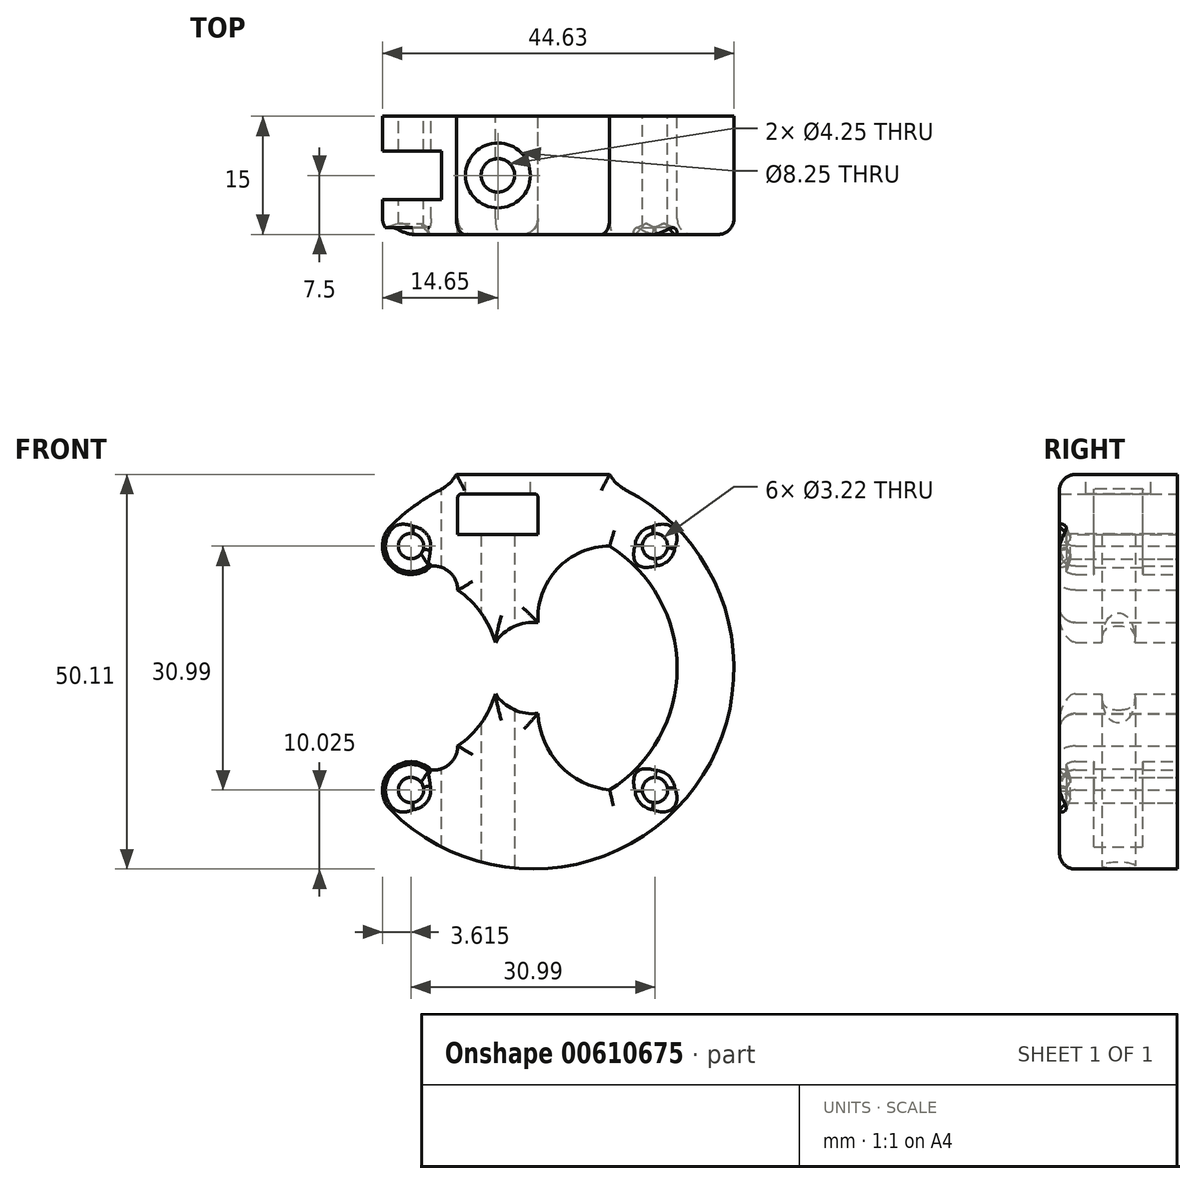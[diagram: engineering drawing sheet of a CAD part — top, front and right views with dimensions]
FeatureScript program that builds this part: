
annotation { "Feature Type Name" : "Feature", "Feature Type Description" : "" }
export const myFeature = defineFeature(function(context is Context, id is Id, definition is map)
    precondition{}
    {
        {
            var Q0;
            Q0=qCreatedBy(makeId("Front.planeOp"),FACE);
            var sketch = newSketch(context, id + "F0", { "sketchPlane" : qUnion([Q0])});
            skLineSegment(sketch, "E0.bottom", {"start": v(15.5, -15.5) * mm, "end": v(-15.5, -15.5) * mm, "construction": true});
            skLineSegment(sketch, "E0.top", {"start": v(15.5, 15.5) * mm, "end": v(-15.5, 15.5) * mm, "construction": true});
            skLineSegment(sketch, "E0.left", {"start": v(15.5, -15.5) * mm, "end": v(15.5, 15.5) * mm, "construction": true});
            skLineSegment(sketch, "E0.right", {"start": v(-15.5, -15.5) * mm, "end": v(-15.5, 15.5) * mm, "construction": true});
            skPoint(sketch, "E0.middle", {"position": v(0, 0) * mm});
            skCircle(sketch, "E1", {"center": v(-15.5, 15.5) * mm, "radius": 1.61 * mm});
            skCircle(sketch, "E2", {"center": v(15.5, 15.5) * mm, "radius": 1.61 * mm});
            skCircle(sketch, "E3", {"center": v(15.5, -15.5) * mm, "radius": 1.61 * mm});
            skCircle(sketch, "E4", {"center": v(-15.5, -15.5) * mm, "radius": 1.61 * mm});
            skArc(sketch, "E5", {"start": v(18.05, 18.05) * mm, "mid": v(14.17, 21.23) * mm, "end": v(9.74, 23.6) * mm});
            skArc(sketch, "E6", {"start": v(12.94, 12.94) * mm, "mid": v(18.05, 12.94) * mm, "end": v(18.05, 18.05) * mm});
            skArc(sketch, "E7", {"start": v(18.05, -18.05) * mm, "mid": v(18.05, -12.94) * mm, "end": v(12.94, -12.94) * mm});
            skArc(sketch, "E8.trimOffspring", {"start": v(-9.74, 15.5) * mm, "mid": v(-18.3, 0) * mm, "end": v(-9.74, -15.5) * mm});
            skLineSegment(sketch, "E9.bottom", {"start": v(-0.64, 22.14) * mm, "end": v(9.56, 22.14) * mm});
            skLineSegment(sketch, "E9.top", {"start": v(-0.64, 16.94) * mm, "end": v(9.56, 16.94) * mm});
            skLineSegment(sketch, "E9.left", {"start": v(-0.64, 22.14) * mm, "end": v(-0.64, 16.94) * mm});
            skLineSegment(sketch, "E9.right", {"start": v(9.56, 22.14) * mm, "end": v(9.56, 16.94) * mm});
            skArc(sketch, "E10.trimOffspring", {"start": v(-9.74, 23.6) * mm, "mid": v(-21.23, -14.17) * mm, "end": v(18.05, -18.05) * mm});
            skLineSegment(sketch, "E11.left", {"start": v(-0.64, 6.98) * mm, "end": v(-0.64, 5.76) * mm});
            skPoint(sketch, "E11.top.end.orphan", {"position": v(9.56, -18.78) * mm});
            skArc(sketch, "E12", {"start": v(-0.64, -5.76) * mm, "mid": v(2.42, -5.27) * mm, "end": v(4.79, -3.27) * mm});
            skArc(sketch, "E13", {"start": v(9.56, 9.9) * mm, "mid": v(6.6, 7) * mm, "end": v(4.79, 3.27) * mm});
            skArc(sketch, "E14.trimOffspring", {"start": v(4.79, -3.27) * mm, "mid": v(6.6, -7) * mm, "end": v(9.56, -9.9) * mm});
            skArc(sketch, "E15.trimOffspring", {"start": v(4.79, 3.27) * mm, "mid": v(2.42, 5.27) * mm, "end": v(-0.64, 5.76) * mm});
            skArc(sketch, "E16", {"start": v(12.94, 12.94) * mm, "mid": v(10.57, 12.18) * mm, "end": v(9.56, 9.9) * mm});
            skArc(sketch, "E17", {"start": v(-0.64, 5.76) * mm, "mid": v(-3.08, 12.6) * mm, "end": v(-9.74, 15.5) * mm});
            skPoint(sketch, "E18.orphan", {"position": v(-0.64, 15.5) * mm});
            skArc(sketch, "E19", {"start": v(9.56, -9.9) * mm, "mid": v(10.57, -12.18) * mm, "end": v(12.94, -12.94) * mm});
            skArc(sketch, "E20", {"start": v(-9.74, -15.5) * mm, "mid": v(-3.4, -12.31) * mm, "end": v(-0.64, -5.76) * mm});
            skLineSegment(sketch, "E21.top", {"start": v(-9.74, 24.6) * mm, "end": v(9.74, 24.6) * mm});
            skLineSegment(sketch, "E21.left", {"start": v(-9.74, 23.6) * mm, "end": v(-9.74, 24.6) * mm});
            skLineSegment(sketch, "E21.right", {"start": v(9.74, 23.6) * mm, "end": v(9.74, 24.6) * mm});
            skSolve(sketch);
        }
        {
            var Q0;
            Q0=makeQuery(id+"F0.imprint","IMPRINT",FACE,{"disambiguationData":[TD([[makeQuery(id+"F0.imprint","IMPRINT",EDGE,{"derivedFrom":sQuery(id+"F0.wireOp",EDGE,"E1")}),-1.0]])]});
            extrude(context, id + "F1", {"entities" : qUnion([Q0]), "depth" : 15 * mm});
        }
        {
            var Q0;
            Q0=makeQuery(id+"F1.opExtrude","SWEPT_EDGE",EDGE,{"disambiguationData":[OSD([sQuery(id+"F0.wireOp",EDGE,"E5"),sQuery(id+"F0.wireOp",EDGE,"E21.right")])]});
            var Q1;
            Q1=makeQuery(id+"F1.opExtrude","SWEPT_EDGE",EDGE,{"disambiguationData":[OSD([sQuery(id+"F0.wireOp",EDGE,"E10.trimOffspring"),sQuery(id+"F0.wireOp",EDGE,"E21.left")])]});
            fillet(context, id + "F2", {"entities" : qUnion([Q0, Q1]), "radius" : 5 * mm, "tangentPropagation" : true, "allowEdgeOverflow" : false});
        }
        {
            var Q0;
            Q0=makeQuery(id+"F1.opExtrude","SWEPT_FACE",FACE,{"disambiguationData":[OSD([sQuery(id+"F0.wireOp",EDGE,"E9.top")])]});
            var sketch = newSketch(context, id + "F3", { "sketchPlane" : qUnion([Q0])});
            skCircle(sketch, "E22", {"center": v(4.46, -7.5) * mm, "radius": 2.12 * mm});
            skPoint(sketch, "E22.centerSnap0", {"position": v(-0.64, -7.5) * mm});
            skPoint(sketch, "E22.centerSnap1", {"position": v(4.46, 0) * mm});
            skSolve(sketch);
        }
        {
            var Q0;
            Q0=makeQuery(id+"F3.imprint","IMPRINT",FACE,{"disambiguationData":[TD([[makeQuery(id+"F3.imprint","IMPRINT",EDGE,{"derivedFrom":sQuery(id+"F3.wireOp",EDGE,"E22")}),1.0]])]});
            extrude(context, id + "F4", {"entities" : qUnion([Q0]), "operationType" : NewBodyOperationType.REMOVE, "endBound" : BoundingType.THROUGH_ALL, "depth" : 60 * mm, "hasSecondDirection" : true, "secondDirectionBound" : SecondDirectionBoundingType.THROUGH_ALL, "secondDirectionOppositeDirection" : true, "secondDirectionDepth" : 25 * mm});
        }
        {
            var Q0;
            Q0=makeQuery(id+"F1.opExtrude","SWEPT_FACE",FACE,{"disambiguationData":[OSD([sQuery(id+"F0.wireOp",EDGE,"E21.top")])]});
            var sketch = newSketch(context, id + "F5", { "sketchPlane" : qUnion([Q0])});
            skCircle(sketch, "E23", {"center": v(4.46, -7.5) * mm, "radius": 4.12 * mm});
            skSolve(sketch);
        }
        {
            var Q0;
            Q0=makeQuery(id+"F5.imprint","IMPRINT",FACE,{"disambiguationData":[TD([[makeQuery(id+"F5.imprint","IMPRINT",EDGE,{"derivedFrom":sQuery(id+"F5.wireOp",EDGE,"E23")}),1.0]])]});
            var Q1;
            Q1=sQuery(id+"F5.wireOp",EDGE,"E23");
            extrude(context, id + "F6", {"entities" : qUnion([Q0]), "operationType" : NewBodyOperationType.REMOVE, "surfaceEntities" : qUnion([Q1]), "endBound" : BoundingType.UP_TO_NEXT, "oppositeDirection" : true, "depth" : 25 * mm});
        }
        {
            var Q0;
            Q0=makeQuery(id+"F1.opExtrude","CAP_EDGE",EDGE,{"disambiguationData":[OSD([sQuery(id+"F0.wireOp",EDGE,"E17")])],"isStart":false});
            var Q1;
            Q1=makeQuery(id+"F1.opExtrude","CAP_EDGE",EDGE,{"disambiguationData":[OSD([sQuery(id+"F0.wireOp",EDGE,"E8.trimOffspring")])],"isStart":false});
            var Q2;
            Q2=makeQuery(id+"F1.opExtrude","CAP_EDGE",EDGE,{"disambiguationData":[OSD([sQuery(id+"F0.wireOp",EDGE,"E15.trimOffspring")])],"isStart":false});
            var Q3;
            Q3=makeQuery(id+"F1.opExtrude","CAP_EDGE",EDGE,{"disambiguationData":[OSD([sQuery(id+"F0.wireOp",EDGE,"E13")])],"isStart":false});
            var Q4;
            Q4=makeQuery(id+"F1.opExtrude","CAP_EDGE",EDGE,{"disambiguationData":[OSD([sQuery(id+"F0.wireOp",EDGE,"E16")])],"isStart":false});
            var Q5;
            Q5=makeQuery(id+"F1.opExtrude","CAP_EDGE",EDGE,{"disambiguationData":[OSD([sQuery(id+"F0.wireOp",EDGE,"E6")])],"isStart":false});
            var Q6;
            Q6=makeQuery(id+"F1.opExtrude","CAP_EDGE",EDGE,{"disambiguationData":[OSD([sQuery(id+"F0.wireOp",EDGE,"E10.trimOffspring")])],"isStart":false});
            var Q7;
            {var subQ0=sQuery(id+"F0.wireOp",EDGE,"E21.left");var subQ1=sQuery(id+"F0.wireOp",EDGE,"E10.trimOffspring");Q7=makeQuery(id+"F2.opFillet","BLEND_EDGE",EDGE,{"blendedFrom":[makeQuery(id+"F1.opExtrude","SWEPT_EDGE",EDGE,{"disambiguationData":[OSD([subQ1,subQ0])]}),makeQuery(id+"F1.opExtrude","CAP_FACE",FACE,{"disambiguationData":[OSD([sQuery(id+"F0.wireOp",EDGE,"E1"),sQuery(id+"F0.wireOp",EDGE,"E2"),sQuery(id+"F0.wireOp",EDGE,"E3"),sQuery(id+"F0.wireOp",EDGE,"E4"),sQuery(id+"F0.wireOp",EDGE,"E5"),sQuery(id+"F0.wireOp",EDGE,"E6"),sQuery(id+"F0.wireOp",EDGE,"E7"),sQuery(id+"F0.wireOp",EDGE,"E8.trimOffspring"),sQuery(id+"F0.wireOp",EDGE,"E9.bottom"),sQuery(id+"F0.wireOp",EDGE,"E9.top"),sQuery(id+"F0.wireOp",EDGE,"E9.left"),sQuery(id+"F0.wireOp",EDGE,"E9.right"),subQ1,sQuery(id+"F0.wireOp",EDGE,"E12"),sQuery(id+"F0.wireOp",EDGE,"E13"),sQuery(id+"F0.wireOp",EDGE,"E14.trimOffspring"),sQuery(id+"F0.wireOp",EDGE,"E15.trimOffspring"),sQuery(id+"F0.wireOp",EDGE,"E16"),sQuery(id+"F0.wireOp",EDGE,"E17"),sQuery(id+"F0.wireOp",EDGE,"E19"),sQuery(id+"F0.wireOp",EDGE,"E20"),sQuery(id+"F0.wireOp",EDGE,"E21.top"),subQ0,sQuery(id+"F0.wireOp",EDGE,"E21.right")])],"isStart":false})],"blendedInto":[makeQuery(id+"F1.opExtrude","CAP_FACE",FACE,{"disambiguationData":[OSD([sQuery(id+"F0.wireOp",EDGE,"E1"),sQuery(id+"F0.wireOp",EDGE,"E2"),sQuery(id+"F0.wireOp",EDGE,"E3"),sQuery(id+"F0.wireOp",EDGE,"E4"),sQuery(id+"F0.wireOp",EDGE,"E5"),sQuery(id+"F0.wireOp",EDGE,"E6"),sQuery(id+"F0.wireOp",EDGE,"E7"),sQuery(id+"F0.wireOp",EDGE,"E8.trimOffspring"),sQuery(id+"F0.wireOp",EDGE,"E9.bottom"),sQuery(id+"F0.wireOp",EDGE,"E9.top"),sQuery(id+"F0.wireOp",EDGE,"E9.left"),sQuery(id+"F0.wireOp",EDGE,"E9.right"),subQ1,sQuery(id+"F0.wireOp",EDGE,"E12"),sQuery(id+"F0.wireOp",EDGE,"E13"),sQuery(id+"F0.wireOp",EDGE,"E14.trimOffspring"),sQuery(id+"F0.wireOp",EDGE,"E15.trimOffspring"),sQuery(id+"F0.wireOp",EDGE,"E16"),sQuery(id+"F0.wireOp",EDGE,"E17"),sQuery(id+"F0.wireOp",EDGE,"E19"),sQuery(id+"F0.wireOp",EDGE,"E20"),sQuery(id+"F0.wireOp",EDGE,"E21.top"),subQ0,sQuery(id+"F0.wireOp",EDGE,"E21.right")])],"isStart":false})]});}
            var Q8;
            Q8=makeQuery(id+"F1.opExtrude","CAP_EDGE",EDGE,{"disambiguationData":[OSD([sQuery(id+"F0.wireOp",EDGE,"E7")])],"isStart":false});
            var Q9;
            Q9=makeQuery(id+"F1.opExtrude","CAP_EDGE",EDGE,{"disambiguationData":[OSD([sQuery(id+"F0.wireOp",EDGE,"E19")])],"isStart":false});
            var Q10;
            Q10=makeQuery(id+"F1.opExtrude","CAP_EDGE",EDGE,{"disambiguationData":[OSD([sQuery(id+"F0.wireOp",EDGE,"E14.trimOffspring")])],"isStart":false});
            var Q11;
            Q11=makeQuery(id+"F1.opExtrude","CAP_EDGE",EDGE,{"disambiguationData":[OSD([sQuery(id+"F0.wireOp",EDGE,"E12")])],"isStart":false});
            var Q12;
            Q12=makeQuery(id+"F1.opExtrude","CAP_EDGE",EDGE,{"disambiguationData":[OSD([sQuery(id+"F0.wireOp",EDGE,"E20")])],"isStart":false});
            var Q13;
            Q13=makeQuery(id+"F1.opExtrude","CAP_EDGE",EDGE,{"disambiguationData":[OSD([sQuery(id+"F0.wireOp",EDGE,"E21.top")])],"isStart":false});
            fillet(context, id + "F7", {"entities" : qUnion([Q0, Q1, Q2, Q3, Q4, Q5, Q6, Q7, Q8, Q9, Q10, Q11, Q12, Q13]), "radius" : 2 * mm, "tangentPropagation" : true, "allowEdgeOverflow" : false});
        }
        {
            var Q0;
            Q0=makeQuery(id+"F1.opExtrude","CAP_EDGE",EDGE,{"disambiguationData":[OSD([sQuery(id+"F0.wireOp",EDGE,"E4")])],"isStart":false});
            var Q1;
            Q1=makeQuery(id+"F1.opExtrude","CAP_EDGE",EDGE,{"disambiguationData":[OSD([sQuery(id+"F0.wireOp",EDGE,"E1")])],"isStart":false});
            var Q2;
            Q2=makeQuery(id+"F1.opExtrude","CAP_EDGE",EDGE,{"disambiguationData":[OSD([sQuery(id+"F0.wireOp",EDGE,"E1")])],"isStart":false});
            var Q3;
            Q3=makeQuery(id+"F1.opExtrude","CAP_EDGE",EDGE,{"disambiguationData":[OSD([sQuery(id+"F0.wireOp",EDGE,"E1")])],"isStart":false});
            var Q4;
            Q4=makeQuery(id+"F1.opExtrude","CAP_EDGE",EDGE,{"disambiguationData":[OSD([sQuery(id+"F0.wireOp",EDGE,"E1")])],"isStart":false});
            var Q5;
            Q5=makeQuery(id+"F1.opExtrude","CAP_EDGE",EDGE,{"disambiguationData":[OSD([sQuery(id+"F0.wireOp",EDGE,"E2")])],"isStart":false});
            var Q6;
            Q6=makeQuery(id+"F7.opFillet","BLEND_EDGE",EDGE,{"blendedFrom":[makeQuery(id+"F1.opExtrude","CAP_EDGE",EDGE,{"disambiguationData":[OSD([sQuery(id+"F0.wireOp",EDGE,"E6")])],"isStart":false}),makeQuery(id+"F1.opExtrude","SWEPT_FACE",FACE,{"disambiguationData":[OSD([sQuery(id+"F0.wireOp",EDGE,"E2")])]})],"blendedInto":[makeQuery(id+"F1.opExtrude","SWEPT_FACE",FACE,{"disambiguationData":[OSD([sQuery(id+"F0.wireOp",EDGE,"E2")])]})]});
            var Q7;
            Q7=makeQuery(id+"F7.opFillet","BLEND_EDGE",EDGE,{"blendedFrom":[makeQuery(id+"F1.opExtrude","CAP_EDGE",EDGE,{"disambiguationData":[OSD([sQuery(id+"F0.wireOp",EDGE,"E7")])],"isStart":false}),makeQuery(id+"F1.opExtrude","SWEPT_FACE",FACE,{"disambiguationData":[OSD([sQuery(id+"F0.wireOp",EDGE,"E3")])]})],"blendedInto":[makeQuery(id+"F1.opExtrude","SWEPT_FACE",FACE,{"disambiguationData":[OSD([sQuery(id+"F0.wireOp",EDGE,"E3")])]})]});
            var Q8;
            Q8=makeQuery(id+"F1.opExtrude","CAP_EDGE",EDGE,{"disambiguationData":[OSD([sQuery(id+"F0.wireOp",EDGE,"E3")])],"isStart":false});
            chamfer(context, id + "F8", {"entities" : qUnion([Q0, Q1, Q2, Q3, Q4, Q5, Q6, Q7, Q8]), "width" : 0.9 * mm, "tangentPropagation" : true});
        }
        {
            var Q0;
            Q0=makeQuery(id+"F1.opExtrude","SWEPT_FACE",FACE,{"disambiguationData":[OSD([sQuery(id+"F0.wireOp",EDGE,"E21.top")])]});
            var sketch = newSketch(context, id + "F9", { "sketchPlane" : qUnion([Q0])});
            skLineSegment(sketch, "E24.bottom", {"start": v(11.6, -4.4) * mm, "end": v(19.1, -4.4) * mm});
            skLineSegment(sketch, "E24.top", {"start": v(11.6, -10.6) * mm, "end": v(19.1, -10.6) * mm});
            skLineSegment(sketch, "E24.left", {"start": v(11.6, -4.4) * mm, "end": v(11.6, -10.6) * mm});
            skLineSegment(sketch, "E24.right", {"start": v(19.1, -4.4) * mm, "end": v(19.1, -10.6) * mm});
            skLineSegment(sketch, "E25", {"start": v(19.1, 0.76) * mm, "end": v(19.1, -13) * mm, "construction": true});
            skLineSegment(sketch, "E26.0", {"start": v(15.16, -15) * mm, "end": v(10.85, -15) * mm, "construction": true});
            skLineSegment(sketch, "E27", {"start": v(4.46, -7.5) * mm, "end": v(22.76, -7.5) * mm, "construction": true});
            skSolve(sketch);
        }
        {
            var Q0;
            Q0=makeQuery(id+"F9.imprint","IMPRINT",FACE,{"disambiguationData":[TD([[makeQuery(id+"F9.imprint","IMPRINT",EDGE,{"derivedFrom":sQuery(id+"F9.wireOp",EDGE,"E24.bottom")}),-1.0]])]});
            extrude(context, id + "F10", {"entities" : qUnion([Q0]), "operationType" : NewBodyOperationType.REMOVE, "endBound" : BoundingType.THROUGH_ALL, "oppositeDirection" : true, "depth" : 25 * mm});
        }
        {
            var Q0;
            Q0=makeQuery(id+"F1.opExtrude","SWEPT_EDGE",EDGE,{"disambiguationData":[OSD([sQuery(id+"F0.wireOp",EDGE,"E9.bottom"),sQuery(id+"F0.wireOp",EDGE,"E9.right")])]});
            var Q1;
            Q1=makeQuery(id+"F1.opExtrude","SWEPT_EDGE",EDGE,{"disambiguationData":[OSD([sQuery(id+"F0.wireOp",EDGE,"E9.bottom"),sQuery(id+"F0.wireOp",EDGE,"E9.left")])]});
            fillet(context, id + "F11", {"entities" : qUnion([Q0, Q1]), "radius" : .5 * mm, "tangentPropagation" : true, "allowEdgeOverflow" : false});
        }
        {
            var Q0;
            Q0=qCreatedBy(makeId("Right.planeOp"),FACE);
            cPlane(context, id + "F12", {"entities" : qUnion([Q0]), "cplaneType" : CPlaneType.OFFSET, "offset" : 25 * mm, "width" : 150 * mm, "height" : 150 * mm});
        }
        {
            var Q0;
            Q0=makeQuery(id+"F1.opExtrude","SWEPT_BODY",BODY,{"disambiguationData":[OSD([sQuery(id+"F0.wireOp",EDGE,"E1"),sQuery(id+"F0.wireOp",EDGE,"E2"),sQuery(id+"F0.wireOp",EDGE,"E3"),sQuery(id+"F0.wireOp",EDGE,"E4"),sQuery(id+"F0.wireOp",EDGE,"E5"),sQuery(id+"F0.wireOp",EDGE,"E6"),sQuery(id+"F0.wireOp",EDGE,"E7"),sQuery(id+"F0.wireOp",EDGE,"E8.trimOffspring"),sQuery(id+"F0.wireOp",EDGE,"E9.bottom"),sQuery(id+"F0.wireOp",EDGE,"E9.top"),sQuery(id+"F0.wireOp",EDGE,"E9.left"),sQuery(id+"F0.wireOp",EDGE,"E9.right"),sQuery(id+"F0.wireOp",EDGE,"E10.trimOffspring"),sQuery(id+"F0.wireOp",EDGE,"E12"),sQuery(id+"F0.wireOp",EDGE,"E13"),sQuery(id+"F0.wireOp",EDGE,"E14.trimOffspring"),sQuery(id+"F0.wireOp",EDGE,"E15.trimOffspring"),sQuery(id+"F0.wireOp",EDGE,"E16"),sQuery(id+"F0.wireOp",EDGE,"E17"),sQuery(id+"F0.wireOp",EDGE,"E19"),sQuery(id+"F0.wireOp",EDGE,"E20"),sQuery(id+"F0.wireOp",EDGE,"E21.top"),sQuery(id+"F0.wireOp",EDGE,"E21.left"),sQuery(id+"F0.wireOp",EDGE,"E21.right")])]});
            var Q1;
            Q1=qCreatedBy(id+"F12.planeOp",FACE);
            mirror(context, id + "F13", {"entities" : qUnion([Q0]), "mirrorPlane" : qUnion([Q1])});
        }
        {
            var Q0;
            Q0=makeQuery(id+"F1.opExtrude","SWEPT_BODY",BODY,{"disambiguationData":[OSD([sQuery(id+"F0.wireOp",EDGE,"E1"),sQuery(id+"F0.wireOp",EDGE,"E2"),sQuery(id+"F0.wireOp",EDGE,"E3"),sQuery(id+"F0.wireOp",EDGE,"E4"),sQuery(id+"F0.wireOp",EDGE,"E5"),sQuery(id+"F0.wireOp",EDGE,"E6"),sQuery(id+"F0.wireOp",EDGE,"E7"),sQuery(id+"F0.wireOp",EDGE,"E8.trimOffspring"),sQuery(id+"F0.wireOp",EDGE,"E9.bottom"),sQuery(id+"F0.wireOp",EDGE,"E9.top"),sQuery(id+"F0.wireOp",EDGE,"E9.left"),sQuery(id+"F0.wireOp",EDGE,"E9.right"),sQuery(id+"F0.wireOp",EDGE,"E10.trimOffspring"),sQuery(id+"F0.wireOp",EDGE,"E12"),sQuery(id+"F0.wireOp",EDGE,"E13"),sQuery(id+"F0.wireOp",EDGE,"E14.trimOffspring"),sQuery(id+"F0.wireOp",EDGE,"E15.trimOffspring"),sQuery(id+"F0.wireOp",EDGE,"E16"),sQuery(id+"F0.wireOp",EDGE,"E17"),sQuery(id+"F0.wireOp",EDGE,"E19"),sQuery(id+"F0.wireOp",EDGE,"E20"),sQuery(id+"F0.wireOp",EDGE,"E21.top"),sQuery(id+"F0.wireOp",EDGE,"E21.left"),sQuery(id+"F0.wireOp",EDGE,"E21.right")])]});
            deleteBodies(context, id + "F14", {"entities" : qUnion([Q0])});
        }
    });
